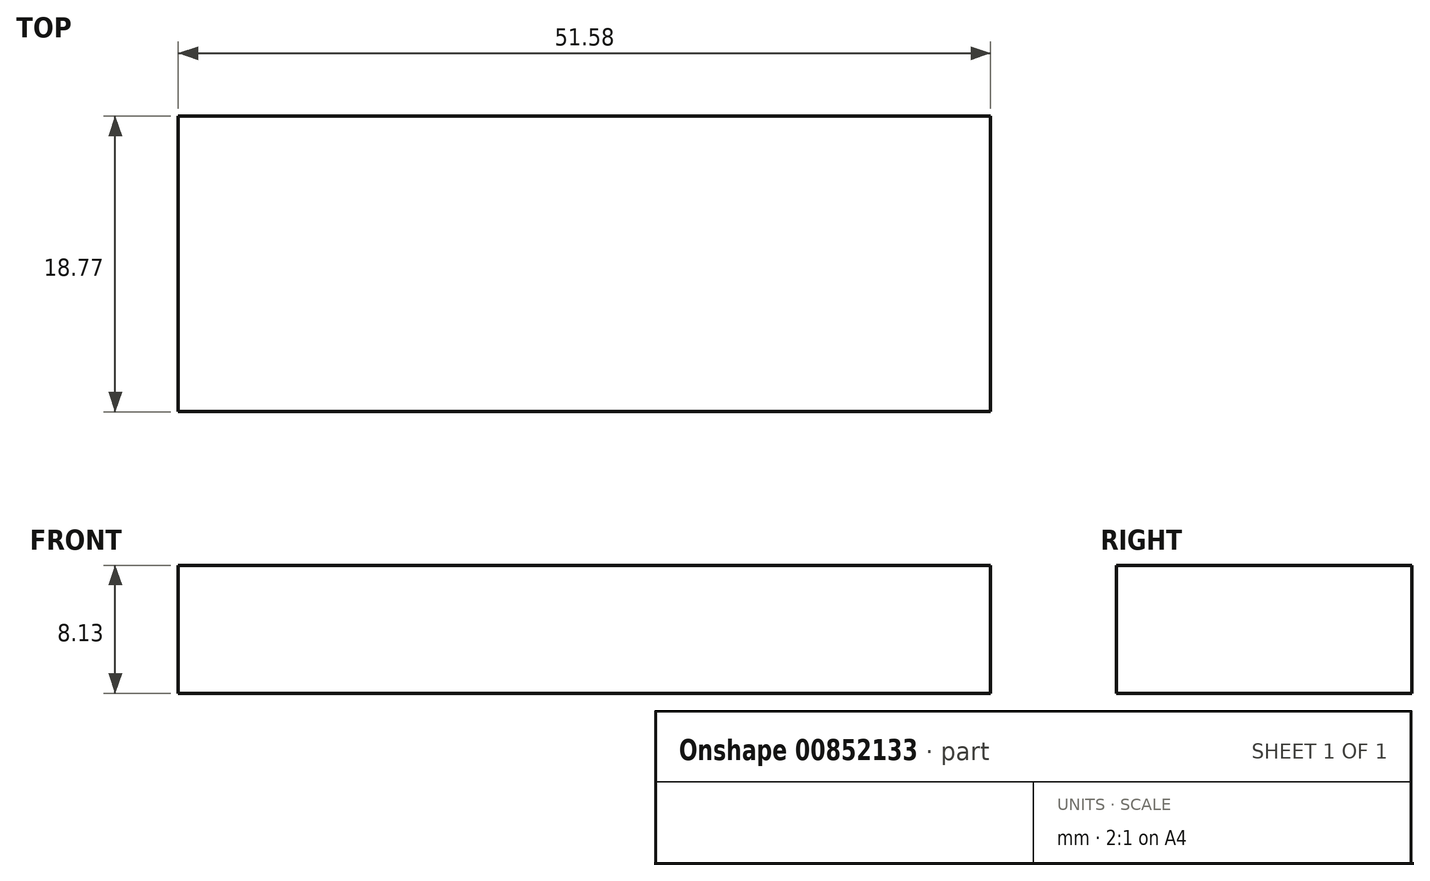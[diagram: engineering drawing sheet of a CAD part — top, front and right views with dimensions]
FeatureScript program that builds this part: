
annotation { "Feature Type Name" : "Feature", "Feature Type Description" : "" }
export const myFeature = defineFeature(function(context is Context, id is Id, definition is map)
    precondition{}
    {
        {
            var Q0;
            Q0=qCreatedBy(makeId("Top.planeOp"),FACE);
            var sketch = newSketch(context, id + "F0", { "sketchPlane" : qUnion([Q0])});
            skLineSegment(sketch, "E0.bottom", {"start": v(-30.54, 4.6) * mm, "end": v(21.04, 4.6) * mm});
            skLineSegment(sketch, "E0.top", {"start": v(-30.54, -14.17) * mm, "end": v(21.04, -14.17) * mm});
            skLineSegment(sketch, "E0.left", {"start": v(-30.54, 4.6) * mm, "end": v(-30.54, -14.17) * mm});
            skLineSegment(sketch, "E0.right", {"start": v(21.04, 4.6) * mm, "end": v(21.04, -14.17) * mm});
            skSolve(sketch);
        }
        {
            var Q0;
            Q0 = qSketchRegion(id + "F0", true);
            extrude(context, id + "F1", {"entities" : qUnion([Q0]), "depth" : 8.13 * mm, "offsetDistance" : 25.4 * mm});
        }
    });
